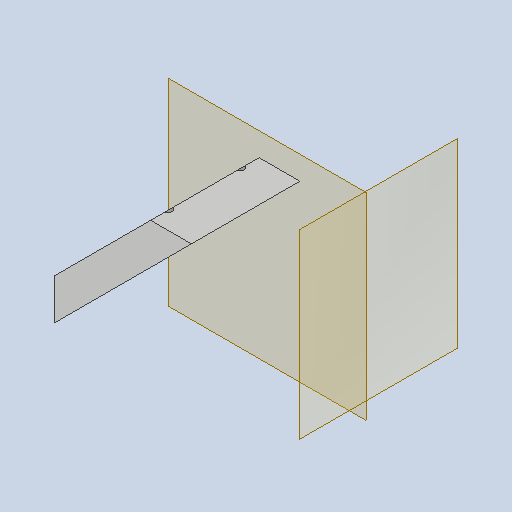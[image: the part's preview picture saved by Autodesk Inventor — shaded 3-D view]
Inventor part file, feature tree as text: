
AUTODESK INVENTOR PART (.ipt)
format: ipt  version: 2023 (Build 270158000, 158)  size: 266,240 bytes
history: native  units: mm
features: reference x16, sketch x9, extrude x8, other x8, plane x4, projected_geometry x4, hole x2
ambient origin geometry x8: Origin, YZ Plane, XZ Plane, XY Plane, X Axis, Y Axis, Z Axis, Center Point
bodies: Solid1 (feature_tree)
feature tree (51):
  plane  "Work Plane1"
  extrude  "Extrusion1"  Depth=53.8mm
  extrude  "Extrusion4"  Depth=53.8mm
  hole  "Hole1"  [1 undecoded]
  extrude  "Extrusion5"  Depth=20.0mm
  plane  "Work Plane3"
  sketch  "Sketch7"  dims[d30=20.0mm d31=20.0mm]
  plane  "Work Plane4"
  extrude  "Extrusion6"  Depth=2.8mm
  extrude  "Extrusion7"  Depth=2.8mm
  hole  "Hole2"  [1 undecoded]
  extrude  "Extrusion8"  Depth=0.1mm
  extrude  "Extrusion9"  Depth=8.0mm
  sketch  "Sketch13"  dims[d40=45.0deg d41=8.0mm d42=28.0mm d43=0.0mm d44=30.0mm d45=20.0mm d46=2.9mm d47=6.0mm d48=6.0mm d49=2.5mm d50=90.0deg d51=12.0mm d52=0.0mm d53=2.0mm d54=28.0mm d55=0.0mm d56=2.0mm d57=28.0mm d58=0.0mm d59=15.0mm d60=10.0mm d61=0.0mm d62=2.8mm d64=2.8mm d65=6.0mm d66=5.5mm d67=3.0mm d68=90.0deg d69=12.0mm d70=0.0mm d71=29.0mm d72=0.0mm d73=4.0mm d74=29.0mm d75=0.0mm d76=10.0mm d77=0.0mm]
  plane  "Work Plane5"
  extrude  "Extrusion10"  Depth=10.0mm TaperAngle=0.0deg
  sketch  "Sketch1"  dims[d10=5.0mm d11=0.0mm d18=53.8mm]
  reference  "Reference1"
  reference  "Reference2"
  reference  "Reference3"
  reference  "Reference4"
  reference  "Reference9"
  reference  "Reference20"
  reference  "Reference21"
  reference  "Reference22"
  reference  "Reference23"
  reference  "Reference24"
  sketch  "Sketch4"  dims[d19=45.0deg d20=53.8mm]
  projected_geometry  "Projected Loop1"
  reference  "Reference25"
  reference  "Reference26"
  projected_geometry  "Projected Loop2"
  sketch  "Sketch6"  dims[d21=45.0mm d22=45.0mm]
  reference  "Reference27"
  reference  "Reference28"
  reference  "Reference29"
  reference  "Reference30"
  sketch  "Sketch8"  dims[d32=2.8mm d33=2.8mm]
  sketch  "Sketch9"  dims[d34=2.8mm d35=2.8mm]
  sketch  "Sketch11"  dims[d36=0.1mm d37=0.1mm]
  projected_geometry  "Projected Loop3"
  sketch  "Sketch12"  dims[d38=0.1mm d39=0.1mm]
  projected_geometry  "Projected Loop5"
  other  "Assembly_Cube_v2_Thorlabs.iam"
  other  "10_Cube_Base:1"
  other  "00_Base_v0:1"
  other  "Assembly_Cube_Kinematic_Mirrormount_45_v2.iam"
  other  "Assembly_Cube_empty_1x1_v2:1"
  other  "10_Cube_1x1_v2:1"
  other  "10_Lid_1x1_v2:1"
  other  "DIN 912 - ersetzt durch DIN EN ISO 4762 M3 x 12:7"
note: 2 required parameter values undecoded (feature->parameter linkage not recoverable at this tier; creation-order binding heuristic only, values carry confidence <= 0.55)
